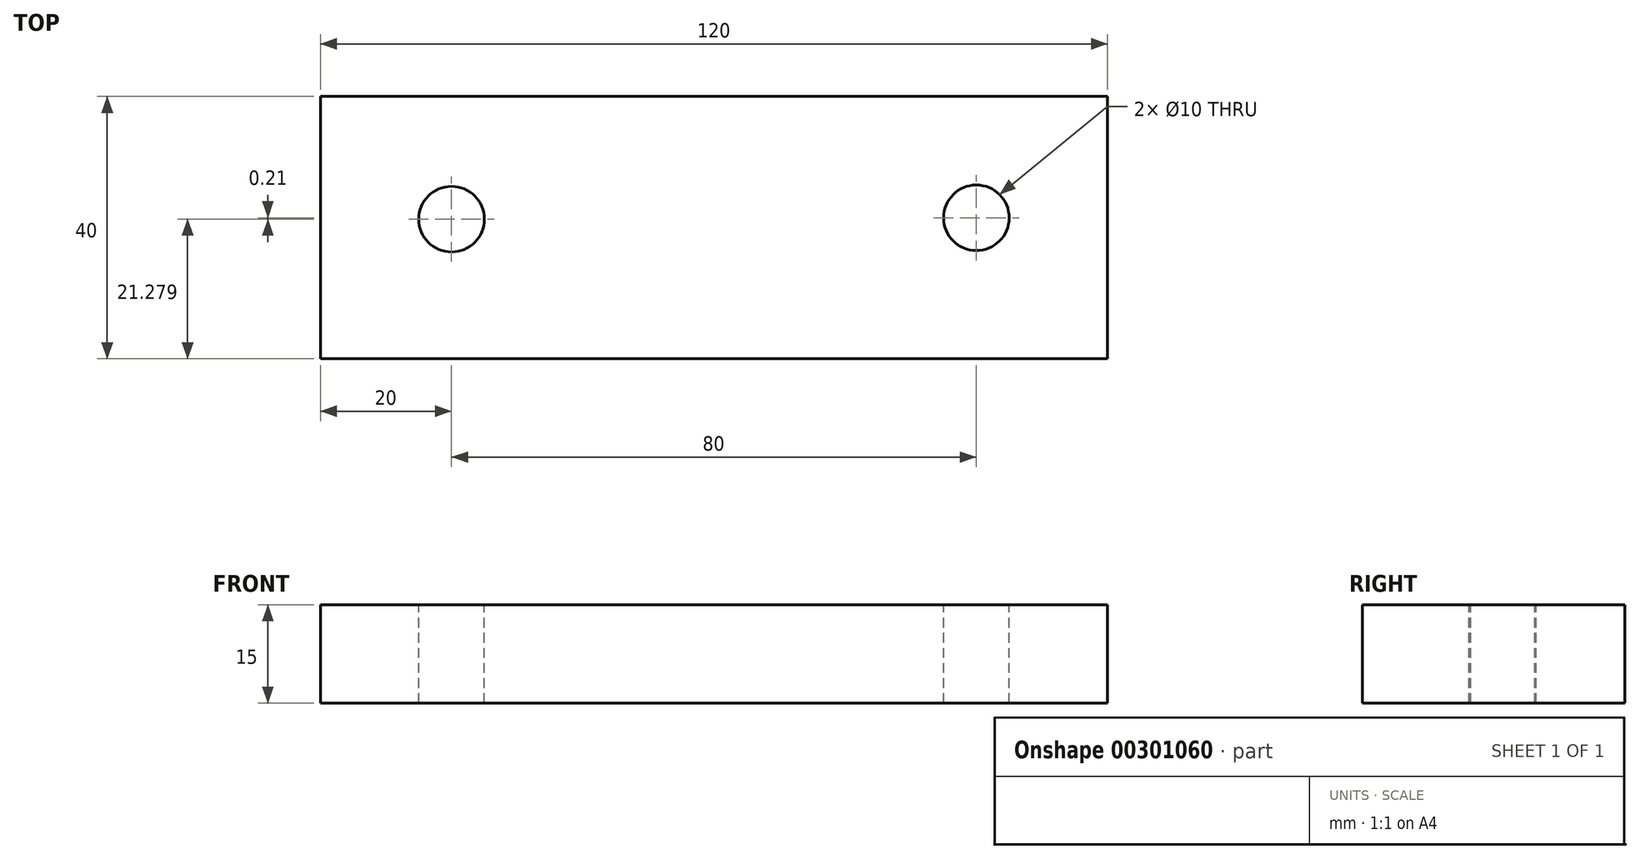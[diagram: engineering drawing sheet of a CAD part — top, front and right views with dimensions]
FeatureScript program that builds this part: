
annotation { "Feature Type Name" : "Feature", "Feature Type Description" : "" }
export const myFeature = defineFeature(function(context is Context, id is Id, definition is map)
    precondition{}
    {
        {
            var Q0;
            Q0=qCreatedBy(makeId("Front.planeOp"),FACE);
            var sketch = newSketch(context, id + "F0", { "sketchPlane" : qUnion([Q0])});
            skLineSegment(sketch, "E0.bottom", {"start": v(0, 0) * mm, "end": v(120, 0) * mm});
            skLineSegment(sketch, "E0.top", {"start": v(0, 15) * mm, "end": v(120, 15) * mm});
            skLineSegment(sketch, "E0.left", {"start": v(0, 0) * mm, "end": v(0, 15) * mm});
            skLineSegment(sketch, "E0.right", {"start": v(120, 0) * mm, "end": v(120, 15) * mm});
            skSolve(sketch);
        }
        {
            var Q0;
            Q0=makeQuery(id+"F0.imprint","IMPRINT",FACE,{"disambiguationData":[TD([[makeQuery(id+"F0.imprint","IMPRINT",EDGE,{"derivedFrom":sQuery(id+"F0.wireOp",EDGE,"E0.bottom")}),1.0]])]});
            extrude(context, id + "F1", {"entities" : qUnion([Q0]), "depth" : 40 * mm});
        }
        {
            var Q0;
            Q0=makeQuery(id+"F1.opExtrude","SWEPT_FACE",FACE,{"disambiguationData":[OSD([sQuery(id+"F0.wireOp",EDGE,"E0.top")])]});
            var sketch = newSketch(context, id + "F2", { "sketchPlane" : qUnion([Q0])});
            skCircle(sketch, "E1", {"center": v(20, -18.72) * mm, "radius": 5 * mm});
            skCircle(sketch, "E2", {"center": v(100, -18.51) * mm, "radius": 5 * mm});
            skSolve(sketch);
        }
        {
            var Q0;
            Q0=makeQuery(id+"F2.imprint","IMPRINT",FACE,{"disambiguationData":[TD([[makeQuery(id+"F2.imprint","IMPRINT",EDGE,{"derivedFrom":sQuery(id+"F2.wireOp",EDGE,"E1")}),1.0]])]});
            var Q1;
            Q1=makeQuery(id+"F2.imprint","IMPRINT",FACE,{"disambiguationData":[TD([[makeQuery(id+"F2.imprint","IMPRINT",EDGE,{"derivedFrom":sQuery(id+"F2.wireOp",EDGE,"E2")}),1.0]])]});
            extrude(context, id + "F3", {"entities" : qUnion([Q0, Q1]), "operationType" : NewBodyOperationType.REMOVE, "endBound" : BoundingType.THROUGH_ALL, "oppositeDirection" : true, "depth" : 25 * mm});
        }
    });
